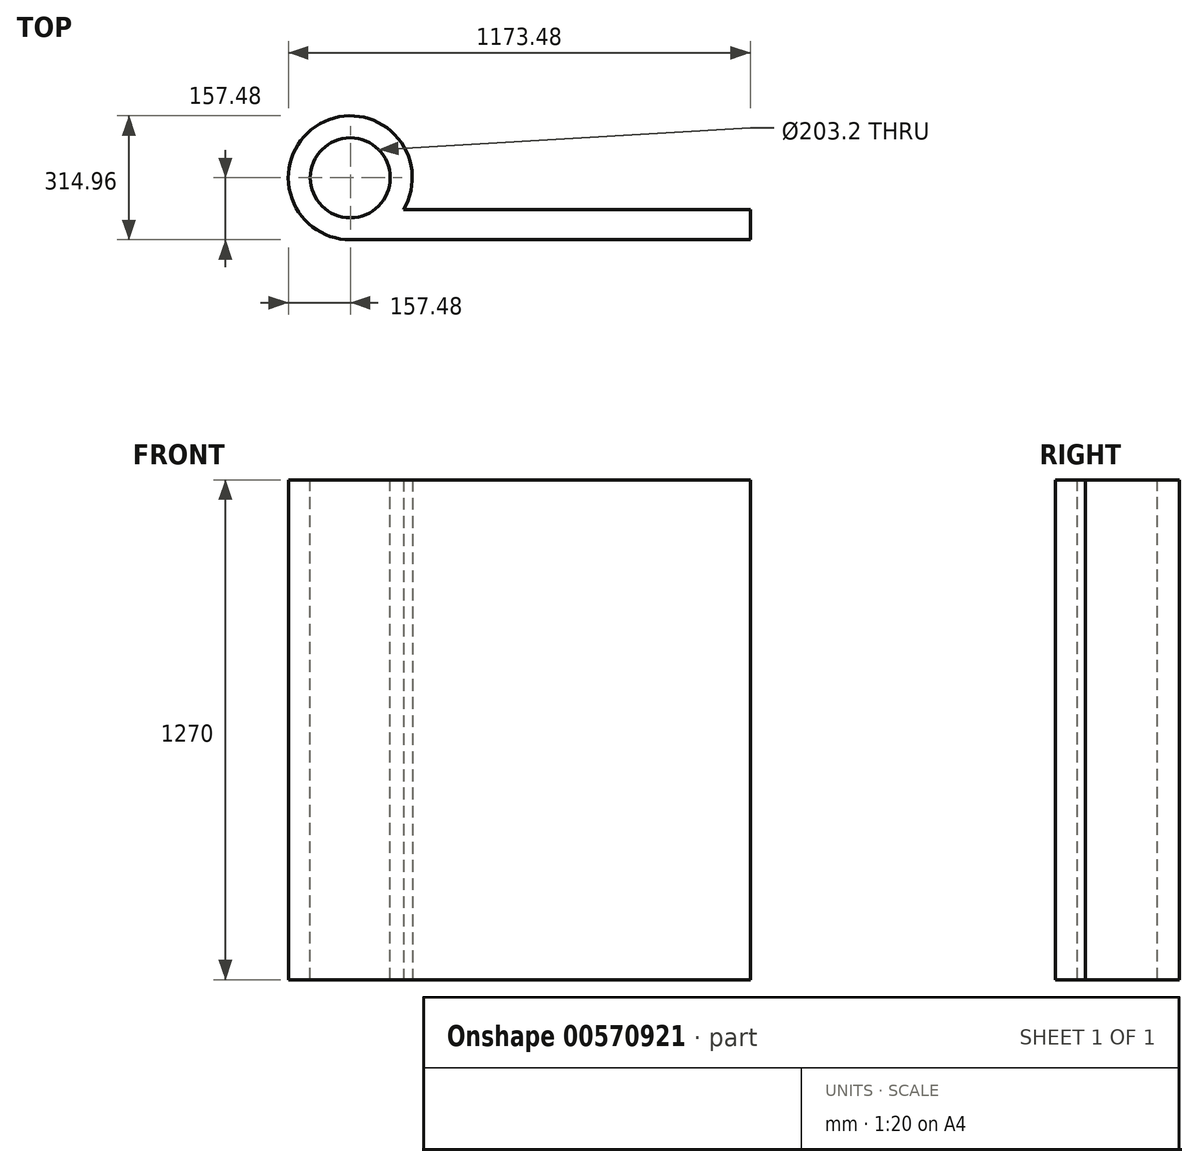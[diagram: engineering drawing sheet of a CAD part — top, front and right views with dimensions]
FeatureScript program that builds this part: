
annotation { "Feature Type Name" : "Feature", "Feature Type Description" : "" }
export const myFeature = defineFeature(function(context is Context, id is Id, definition is map)
    precondition{}
    {
        {
            var Q0;
            Q0=qCreatedBy(makeId("Top.planeOp"),FACE);
            var sketch = newSketch(context, id + "F0", { "sketchPlane" : qUnion([Q0])});
            skLineSegment(sketch, "E0", {"start": v(0, 0) * mm, "end": v(1016, 0) * mm});
            skLineSegment(sketch, "E1", {"start": v(1016, 0) * mm, "end": v(1016, 76.2) * mm});
            skLineSegment(sketch, "E2", {"start": v(1016, 76.2) * mm, "end": v(134.88, 76.2) * mm});
            skLineSegment(sketch, "E3", {"start": v(0, 0) * mm, "end": v(0, 343.53) * mm, "construction": true});
            skPoint(sketch, "E4", {"position": v(0, 157.48) * mm});
            skArc(sketch, "E5", {"start": v(0, 0) * mm, "mid": v(-77.46, 294.6) * mm, "end": v(134.88, 76.2) * mm});
            skSolve(sketch);
        }
        {
            var Q0;
            Q0=makeQuery(id+"F0.imprint","IMPRINT",FACE,{"disambiguationData":[TD([[makeQuery(id+"F0.imprint","IMPRINT",EDGE,{"derivedFrom":sQuery(id+"F0.wireOp",EDGE,"E0")}),1.0]])]});
            extrude(context, id + "F1", {"entities" : qUnion([Q0]), "depth" : 1270 * mm, "offsetDistance" : 25.4 * mm});
        }
        {
            var Q0;
            Q0=makeQuery(id+"F1.opExtrude","CAP_FACE",FACE,{"disambiguationData":[OSD([sQuery(id+"F0.wireOp",EDGE,"E0"),sQuery(id+"F0.wireOp",EDGE,"E1"),sQuery(id+"F0.wireOp",EDGE,"E2"),sQuery(id+"F0.wireOp",EDGE,"E5")])],"isStart":false});
            var sketch = newSketch(context, id + "F2", { "sketchPlane" : qUnion([Q0])});
            skCircle(sketch, "E6", {"center": v(0, 157.48) * mm, "radius": 101.6 * mm});
            skSolve(sketch);
        }
        {
            var Q0;
            Q0 = qSketchRegion(id + "F2", true);
            extrude(context, id + "F3", {"entities" : qUnion([Q0]), "operationType" : NewBodyOperationType.REMOVE, "endBound" : BoundingType.THROUGH_ALL, "oppositeDirection" : true, "depth" : 25.4 * mm, "offsetDistance" : 25.4 * mm});
        }
    });
